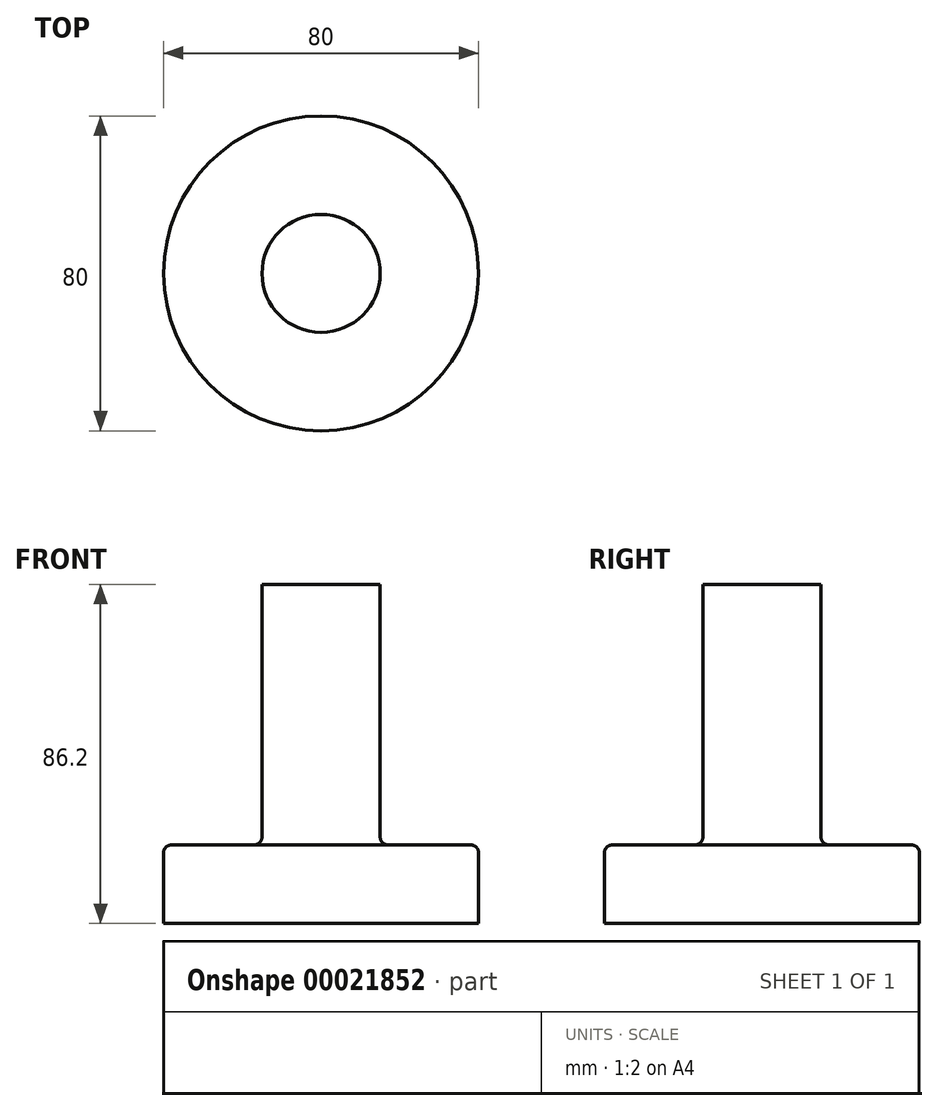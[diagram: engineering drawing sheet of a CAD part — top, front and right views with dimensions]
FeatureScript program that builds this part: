
annotation { "Feature Type Name" : "Feature", "Feature Type Description" : "" }
export const myFeature = defineFeature(function(context is Context, id is Id, definition is map)
    precondition{}
    {
        {
            var Q0;
            Q0=qCreatedBy(makeId("Front.planeOp"),FACE);
            var sketch = newSketch(context, id + "F0", { "sketchPlane" : qUnion([Q0])});
            skLineSegment(sketch, "E0", {"start": v(0, 0) * mm, "end": v(-40, 0) * mm});
            skLineSegment(sketch, "E1", {"start": v(-40, 0) * mm, "end": v(-40, 20) * mm});
            skLineSegment(sketch, "E2", {"start": v(-40, 20) * mm, "end": v(-15, 20) * mm});
            skLineSegment(sketch, "E3", {"start": v(-15, 20) * mm, "end": v(-15, 86.2) * mm});
            skLineSegment(sketch, "E4", {"start": v(-15, 86.2) * mm, "end": v(0, 86.2) * mm});
            skLineSegment(sketch, "E5", {"start": v(0, 86.2) * mm, "end": v(0, 0) * mm});
            skSolve(sketch);
        }
        {
            var Q0;
            Q0=makeQuery(id+"F0.imprint","IMPRINT",FACE,{"disambiguationData":[TD([[makeQuery(id+"F0.imprint","IMPRINT",EDGE,{"derivedFrom":sQuery(id+"F0.wireOp",EDGE,"E0")}),-1.0]])]});
            var Q1;
            Q1=sQuery(id+"F0.wireOp",EDGE,"E5");
            revolve(context, id + "F1", {"entities" : qUnion([Q0]), "axis" : qUnion([Q1]), "revolveType" : RevolveType.FULL});
        }
        {
            var Q0;
            Q0=makeQuery(id+"F1.opRevolve","SWEPT_EDGE",EDGE,{"disambiguationData":[OSD([sQuery(id+"F0.wireOp",EDGE,"E1"),sQuery(id+"F0.wireOp",EDGE,"E2")])]});
            var Q1;
            Q1=makeQuery(id+"F1.opRevolve","SWEPT_EDGE",EDGE,{"disambiguationData":[OSD([sQuery(id+"F0.wireOp",EDGE,"E2"),sQuery(id+"F0.wireOp",EDGE,"E3")])]});
            fillet(context, id + "F2", {"entities" : qUnion([Q0, Q1]), "radius" : 2 * mm, "tangentPropagation" : true, "allowEdgeOverflow" : false});
        }
    });
